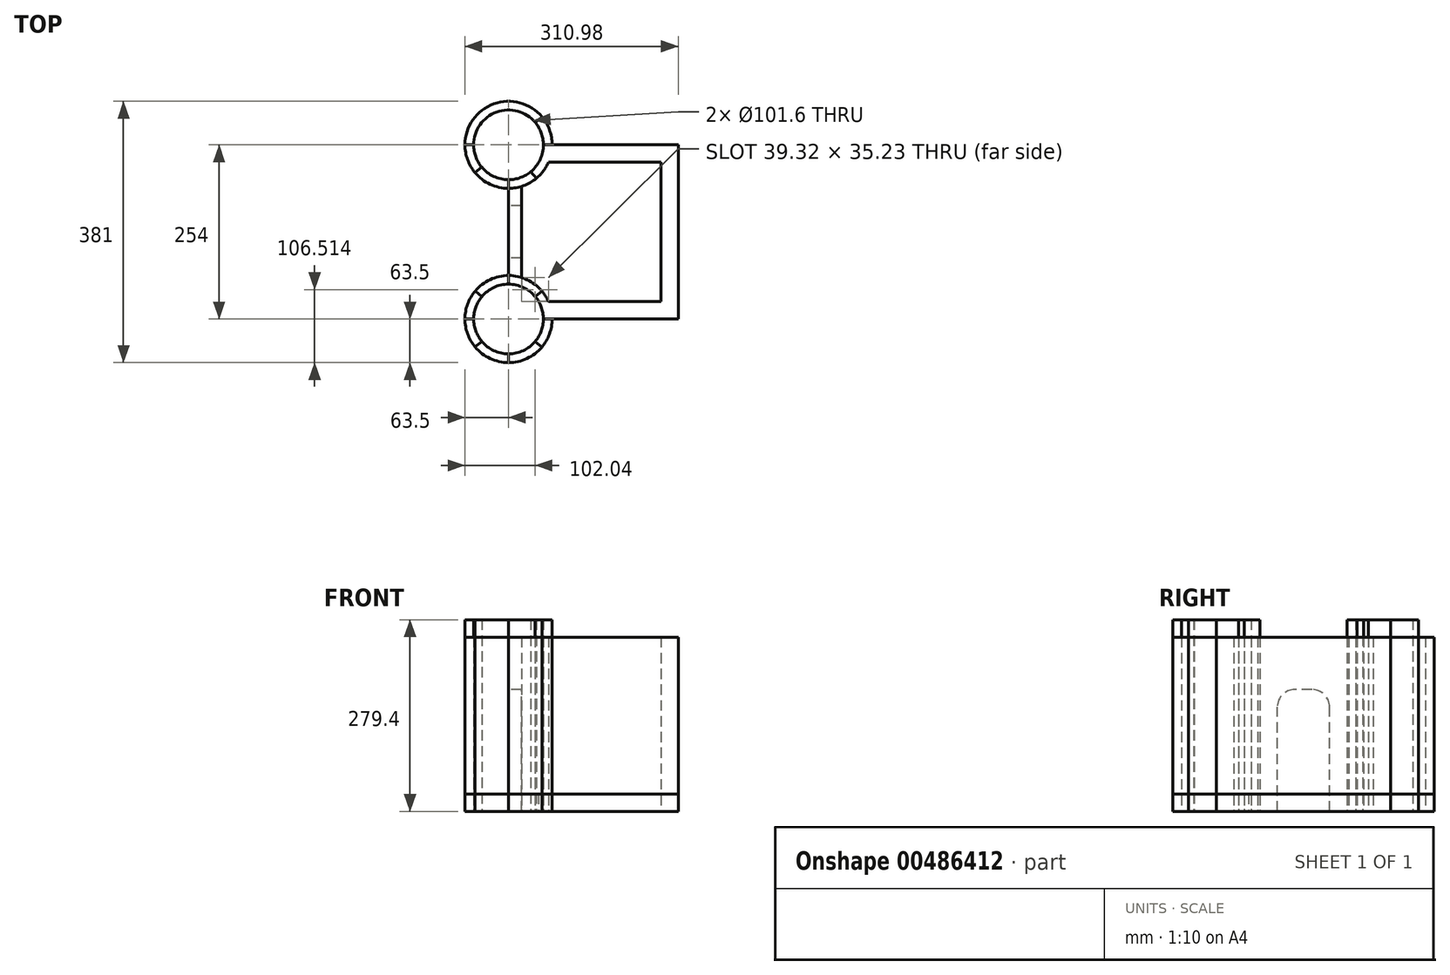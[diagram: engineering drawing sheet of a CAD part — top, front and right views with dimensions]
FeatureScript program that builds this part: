
annotation { "Feature Type Name" : "Feature", "Feature Type Description" : "" }
export const myFeature = defineFeature(function(context is Context, id is Id, definition is map)
    precondition{}
    {
        {
            var Q0;
            Q0=qCreatedBy(makeId("Top.planeOp"),FACE);
            var sketch = newSketch(context, id + "F0", { "sketchPlane" : qUnion([Q0])});
            skLineSegment(sketch, "E0.bottom", {"start": v(-63.5, 127) * mm, "end": v(120.48, 127) * mm});
            skLineSegment(sketch, "E0.top", {"start": v(-63.5, -127) * mm, "end": v(120.48, -127) * mm});
            skLineSegment(sketch, "E0.left", {"start": v(-127, 63.5) * mm, "end": v(-127, -63.5) * mm});
            skLineSegment(sketch, "E0.right", {"start": v(120.48, 127) * mm, "end": v(120.48, -127) * mm});
            skCircle(sketch, "E1", {"center": v(-127, -127) * mm, "radius": 63.5 * mm});
            skCircle(sketch, "E2", {"center": v(-127, 127) * mm, "radius": 63.5 * mm});
            skCircle(sketch, "E3", {"center": v(-127, 127) * mm, "radius": 50.8 * mm});
            skCircle(sketch, "E4", {"center": v(-127, -127) * mm, "radius": 50.8 * mm});
            skLineSegment(sketch, "E5", {"start": v(-127, 76.2) * mm, "end": v(-127, 63.5) * mm});
            skLineSegment(sketch, "E6", {"start": v(-76.2, 127) * mm, "end": v(-63.5, 127) * mm});
            skLineSegment(sketch, "E7", {"start": v(-127, 177.8) * mm, "end": v(-127, 190.5) * mm});
            skLineSegment(sketch, "E8", {"start": v(-127, 190.5) * mm, "end": v(-127, 177.8) * mm});
            skLineSegment(sketch, "E9", {"start": v(-190.5, 127) * mm, "end": v(-177.8, 127) * mm});
            skLineSegment(sketch, "E10", {"start": v(-159.5, 166.04) * mm, "end": v(-167.64, 175.8) * mm});
            skLineSegment(sketch, "E11", {"start": v(-167.64, 175.8) * mm, "end": v(-159.5, 166.04) * mm});
            skLineSegment(sketch, "E12", {"start": v(-94.5, 87.96) * mm, "end": v(-86.36, 78.2) * mm});
            skLineSegment(sketch, "E13", {"start": v(-87.96, 159.5) * mm, "end": v(-78.2, 167.64) * mm});
            skLineSegment(sketch, "E14", {"start": v(-78.2, 167.64) * mm, "end": v(-87.96, 159.5) * mm});
            skLineSegment(sketch, "E15", {"start": v(-166.04, 94.5) * mm, "end": v(-175.8, 86.36) * mm});
            skLineSegment(sketch, "E16", {"start": v(-127, -63.5) * mm, "end": v(-127, -76.2) * mm});
            skLineSegment(sketch, "E17", {"start": v(-63.5, -127) * mm, "end": v(-76.2, -127) * mm});
            skLineSegment(sketch, "E18", {"start": v(-88.14, -159.72) * mm, "end": v(-78.43, -167.9) * mm});
            skLineSegment(sketch, "E19", {"start": v(-78.43, -167.9) * mm, "end": v(-88.14, -159.72) * mm});
            skLineSegment(sketch, "E20", {"start": v(-88.05, -94.38) * mm, "end": v(-78.32, -86.23) * mm});
            skLineSegment(sketch, "E21", {"start": v(-78.32, -86.23) * mm, "end": v(-88.05, -94.38) * mm});
            skLineSegment(sketch, "E22.trimOffspring", {"start": v(-165.95, -159.62) * mm, "end": v(-175.68, -167.77) * mm});
            skLineSegment(sketch, "E23.trimOffspring", {"start": v(-165.86, -94.28) * mm, "end": v(-175.57, -86.1) * mm});
            skLineSegment(sketch, "E24.trimOffspring", {"start": v(-127, -177.8) * mm, "end": v(-127, -190.5) * mm});
            skLineSegment(sketch, "E25.trimOffspring", {"start": v(-177.8, -127) * mm, "end": v(-190.5, -127) * mm});
            skLineSegment(sketch, "E26.bottom", {"start": v(95.08, -101.6) * mm, "end": v(-68.8, -101.6) * mm});
            skLineSegment(sketch, "E26.top", {"start": v(95.08, 101.6) * mm, "end": v(-68.8, 101.6) * mm});
            skLineSegment(sketch, "E26.left", {"start": v(95.08, -101.6) * mm, "end": v(95.08, 101.6) * mm});
            skLineSegment(sketch, "E26.right", {"start": v(-108.12, -66.37) * mm, "end": v(-108.12, 66.37) * mm});
            skSolve(sketch);
        }
        {
            var Q0;
            {var subQ0=sQuery(id+"F0.wireOp",EDGE,"E23.trimOffspring");Q0=makeQuery(id+"F0.imprint","IMPRINT",FACE,{"disambiguationData":[TD([[makeQuery(id+"F0.imprint","IMPRINT",EDGE,{"derivedFrom":subQ0}),1.0]])]});}
            var Q1;
            {var subQ0=sQuery(id+"F0.wireOp",EDGE,"E22.trimOffspring");Q1=makeQuery(id+"F0.imprint","IMPRINT",FACE,{"disambiguationData":[TD([[makeQuery(id+"F0.imprint","IMPRINT",EDGE,{"derivedFrom":subQ0}),1.0]])]});}
            var Q2;
            {var subQ0=sQuery(id+"F0.wireOp",EDGE,"E17");Q2=makeQuery(id+"F0.imprint","IMPRINT",FACE,{"disambiguationData":[TD([[makeQuery(id+"F0.imprint","IMPRINT",EDGE,{"derivedFrom":subQ0}),1.0]])]});}
            var Q3;
            {var subQ0=sQuery(id+"F0.wireOp",EDGE,"E8");Q3=makeQuery(id+"F0.imprint","IMPRINT",FACE,{"disambiguationData":[TD([[makeQuery(id+"F0.imprint","IMPRINT",EDGE,{"derivedFrom":subQ0}),-1.0]])]});}
            var Q4;
            {var subQ0=sQuery(id+"F0.wireOp",EDGE,"E9");Q4=makeQuery(id+"F0.imprint","IMPRINT",FACE,{"disambiguationData":[TD([[makeQuery(id+"F0.imprint","IMPRINT",EDGE,{"derivedFrom":subQ0}),-1.0]])]});}
            var Q5;
            {var subQ0=sQuery(id+"F0.wireOp",EDGE,"E16");Q5=makeQuery(id+"F0.imprint","IMPRINT",FACE,{"disambiguationData":[TD([[makeQuery(id+"F0.imprint","IMPRINT",EDGE,{"derivedFrom":subQ0}),1.0]])]});}
            var Q6;
            {var subQ3=sQuery(id+"F0.wireOp",EDGE,"E5");Q6=makeQuery(id+"F0.imprint","IMPRINT",FACE,{"disambiguationData":[TD([[makeQuery(id+"F0.imprint","IMPRINT",EDGE,{"derivedFrom":subQ3}),1.0]])]});}
            var Q7;
            {var subQ0=sQuery(id+"F0.wireOp",EDGE,"E6");Q7=makeQuery(id+"F0.imprint","IMPRINT",FACE,{"disambiguationData":[TD([[makeQuery(id+"F0.imprint","IMPRINT",EDGE,{"derivedFrom":subQ0}),1.0]])]});}
            extrude(context, id + "F1", {"entities" : qUnion([Q0, Q1, Q2, Q3, Q4, Q5, Q6, Q7]), "depth" : 279.4 * mm});
        }
        {
            var Q0;
            Q0 = qSketchRegion(id + "F0", true);
            extrude(context, id + "F2", {"entities" : qUnion([Q0]), "depth" : 254 * mm});
        }
        {
            var Q0;
            Q0=makeQuery(id+"F2.opExtrude","SWEPT_FACE",FACE,{"disambiguationData":[OSD([sQuery(id+"F0.wireOp",EDGE,"E0.left")])]});
            var sketch = newSketch(context, id + "F3", { "sketchPlane" : qUnion([Q0])});
            skLineSegment(sketch, "E27", {"start": v(38.1, 0) * mm, "end": v(38.1, 152.4) * mm});
            skLineSegment(sketch, "E28", {"start": v(-38.1, 0) * mm, "end": v(-38.1, 152.4) * mm});
            skLineSegment(sketch, "E29", {"start": v(-12.7, 177.8) * mm, "end": v(12.7, 177.8) * mm});
            skPoint(sketch, "E30.visualSharp", {"position": v(-38.1, 177.8) * mm});
            skArc(sketch, "E30.filletArc", {"start": v(-12.7, 177.8) * mm, "mid": v(-30.66, 170.36) * mm, "end": v(-38.1, 152.4) * mm});
            skPoint(sketch, "E31.visualSharp", {"position": v(38.1, 177.8) * mm});
            skArc(sketch, "E31.filletArc", {"start": v(38.1, 152.4) * mm, "mid": v(30.66, 170.36) * mm, "end": v(12.7, 177.8) * mm});
            skLineSegment(sketch, "E32", {"start": v(-38.1, 0) * mm, "end": v(38.1, 0) * mm});
            skSolve(sketch);
        }
        {
            var Q0;
            Q0=makeQuery(id+"F3.imprint","IMPRINT",FACE,{"disambiguationData":[TD([[makeQuery(id+"F3.imprint","IMPRINT",EDGE,{"derivedFrom":sQuery(id+"F3.wireOp",EDGE,"E27")}),1.0]])]});
            extrude(context, id + "F4", {"entities" : qUnion([Q0]), "operationType" : NewBodyOperationType.REMOVE, "oppositeDirection" : true, "depth" : 25.4 * mm});
        }
        {
            var Q0;
            Q0=makeQuery(id+"F2.opExtrude","CAP_FACE",FACE,{"disambiguationData":[OSD([sQuery(id+"F0.wireOp",EDGE,"E0.bottom"),sQuery(id+"F0.wireOp",EDGE,"E0.top"),sQuery(id+"F0.wireOp",EDGE,"E0.left"),sQuery(id+"F0.wireOp",EDGE,"E0.right"),sQuery(id+"F0.wireOp",EDGE,"E1"),sQuery(id+"F0.wireOp",EDGE,"E2"),sQuery(id+"F0.wireOp",EDGE,"E3"),sQuery(id+"F0.wireOp",EDGE,"E4"),sQuery(id+"F0.wireOp",EDGE,"E26.bottom"),sQuery(id+"F0.wireOp",EDGE,"E26.top"),sQuery(id+"F0.wireOp",EDGE,"E26.left"),sQuery(id+"F0.wireOp",EDGE,"E26.right")])],"isStart":true});
            var sketch = newSketch(context, id + "F5", { "sketchPlane" : qUnion([Q0])});
            skLineSegment(sketch, "E33.bottom", {"start": v(95.08, -101.6) * mm, "end": v(-83, -101.6) * mm});
            skLineSegment(sketch, "E33.top", {"start": v(95.08, 101.6) * mm, "end": v(-83, 101.6) * mm});
            skLineSegment(sketch, "E33.left", {"start": v(95.08, -101.6) * mm, "end": v(95.08, 101.6) * mm});
            skLineSegment(sketch, "E33.right", {"start": v(-108.12, -79.84) * mm, "end": v(-108.12, -38.1) * mm});
            skLineSegment(sketch, "E34.bottom", {"start": v(-127, 38.1) * mm, "end": v(-108.12, 38.1) * mm});
            skLineSegment(sketch, "E34.top", {"start": v(-127, -38.1) * mm, "end": v(-108.12, -38.1) * mm});
            skLineSegment(sketch, "E34.left", {"start": v(-127, 38.1) * mm, "end": v(-127, -38.1) * mm});
            skLineSegment(sketch, "E35.trimOffspring", {"start": v(-108.12, 38.1) * mm, "end": v(-108.12, 79.84) * mm});
            skArc(sketch, "E36", {"start": v(-83, 101.6) * mm, "mid": v(-160.27, 165.4) * mm, "end": v(-108.12, 79.84) * mm});
            skArc(sketch, "E37", {"start": v(-108.12, -79.84) * mm, "mid": v(-160.27, -165.4) * mm, "end": v(-83, -101.6) * mm});
            skSolve(sketch);
        }
        {
            var Q0;
            {var subQ0=sQuery(id+"F5.wireOp",EDGE,"E36");Q0=makeQuery(id+"F5.imprint","IMPRINT",FACE,{"disambiguationData":[TD([[makeQuery(id+"F5.imprint","IMPRINT",EDGE,{"derivedFrom":subQ0}),-1.0]])]});}
            var Q1;
            {var subQ0=sQuery(id+"F5.wireOp",EDGE,"E37");Q1=makeQuery(id+"F5.imprint","IMPRINT",FACE,{"disambiguationData":[TD([[makeQuery(id+"F5.imprint","IMPRINT",EDGE,{"derivedFrom":subQ0}),-1.0]])]});}
            var Q2;
            {var subQ1=sQuery(id+"F0.wireOp",EDGE,"E2");var subQ2=makeQuery(id+"F0.imprint","INTERSECT",VERTEX,{"derivedFrom":[subQ1,sQuery(id+"F0.wireOp",EDGE,"E12")]});var subQ3=makeQuery(id+"F2.opExtrude","CAP_EDGE",EDGE,{"disambiguationData":[OSD([subQ1]),TDD([makeQuery(id+"F0.imprint","IMPRINT",EDGE,{"disambiguationData":[TD([[subQ2,1.0]])],"derivedFrom":subQ1}),makeQuery(id+"F0.imprint","IMPRINT",EDGE,{"disambiguationData":[TD([[subQ2,-1.0]])],"derivedFrom":subQ1})])],"isStart":true});Q2=makeQuery(id+"F5.imprint","IMPRINT",FACE,{"disambiguationData":[TD([[makeQuery(id+"F5.imprint","IMPRINT",EDGE,{"derivedFrom":subQ3}),-1.0]])]});}
            var Q3;
            {var subQ1=sQuery(id+"F0.wireOp",EDGE,"E1");var subQ2=makeQuery(id+"F0.imprint","INTERSECT",VERTEX,{"derivedFrom":[subQ1,sQuery(id+"F0.wireOp",EDGE,"E21")]});var subQ3=makeQuery(id+"F2.opExtrude","CAP_EDGE",EDGE,{"disambiguationData":[OSD([subQ1]),TDD([makeQuery(id+"F0.imprint","IMPRINT",EDGE,{"disambiguationData":[TD([[subQ2,1.0]])],"derivedFrom":subQ1}),makeQuery(id+"F0.imprint","IMPRINT",EDGE,{"disambiguationData":[TD([[subQ2,-1.0]])],"derivedFrom":subQ1})])],"isStart":true});Q3=makeQuery(id+"F5.imprint","IMPRINT",FACE,{"disambiguationData":[TD([[makeQuery(id+"F5.imprint","IMPRINT",EDGE,{"derivedFrom":subQ3}),-1.0]])]});}
            var Q4;
            {var subQ9=sQuery(id+"F5.wireOp",EDGE,"E33.left");Q4=makeQuery(id+"F5.imprint","IMPRINT",FACE,{"disambiguationData":[TD([[makeQuery(id+"F5.imprint","IMPRINT",EDGE,{"derivedFrom":subQ9}),-1.0]])]});}
            extrude(context, id + "F6", {"entities" : qUnion([Q0, Q1, Q2, Q3, Q4]), "oppositeDirection" : true, "depth" : 25.4 * mm});
        }
    });
